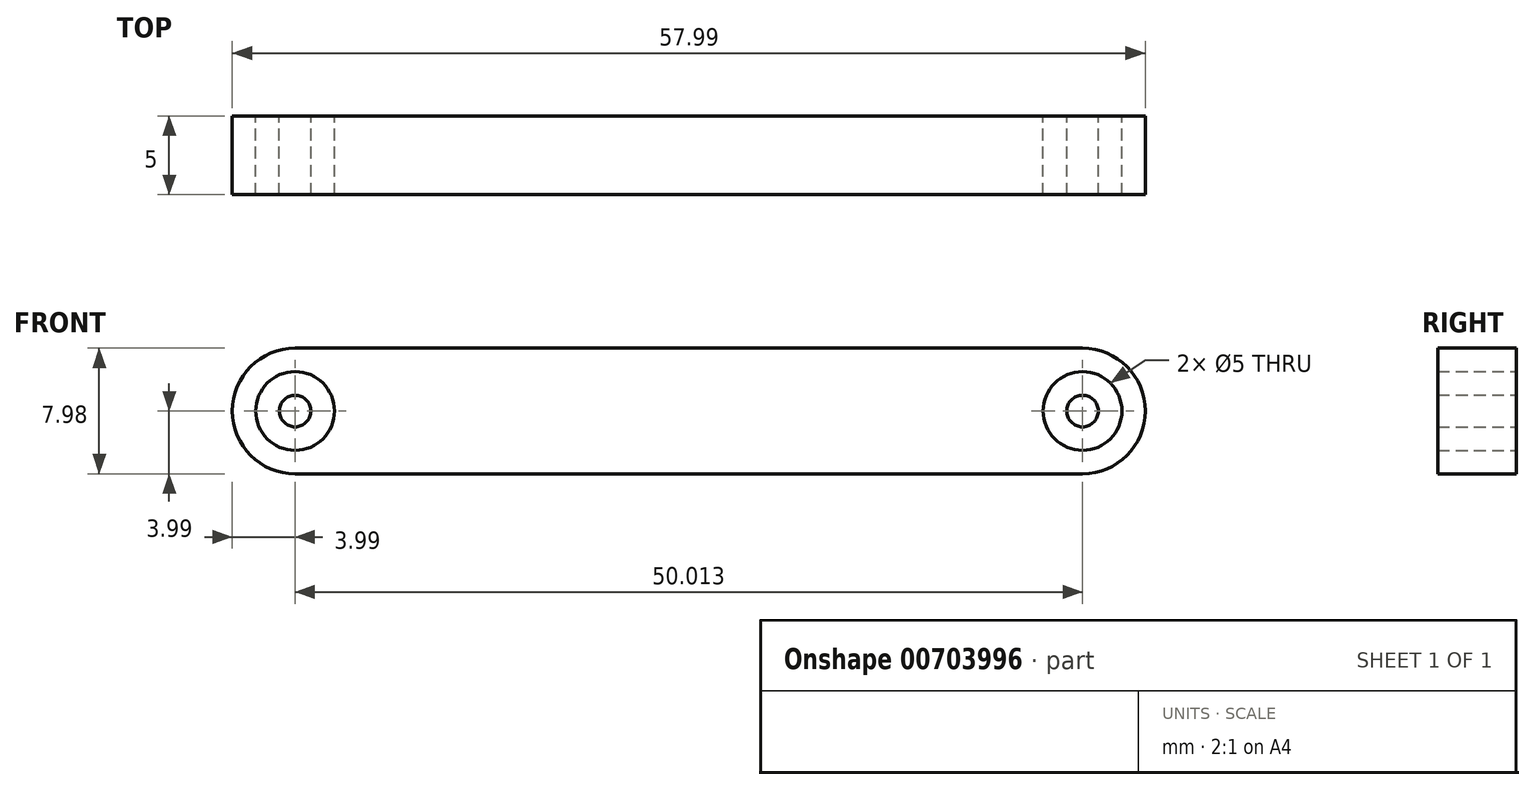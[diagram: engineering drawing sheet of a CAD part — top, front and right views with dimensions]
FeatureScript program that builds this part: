
annotation { "Feature Type Name" : "Feature", "Feature Type Description" : "" }
export const myFeature = defineFeature(function(context is Context, id is Id, definition is map)
    precondition{}
    {
        {
            var Q0;
            Q0=qCreatedBy(makeId("Front.planeOp"),FACE);
            var sketch = newSketch(context, id + "F0", { "sketchPlane" : qUnion([Q0])});
            skCircle(sketch, "E0", {"center": v(0, 0) * mm, "radius": 2.5 * mm});
            skCircle(sketch, "E1", {"center": v(0, 0) * mm, "radius": 1 * mm});
            skArc(sketch, "E2", {"start": v(0, -3.99) * mm, "mid": v(-3.99, 0) * mm, "end": v(0, 3.99) * mm});
            skCircle(sketch, "E3", {"center": v(50.01, 0) * mm, "radius": 1 * mm});
            skCircle(sketch, "E4", {"center": v(50.01, 0) * mm, "radius": 2.5 * mm});
            skArc(sketch, "E5", {"start": v(50.01, -3.99) * mm, "mid": v(54, 0) * mm, "end": v(50.01, 3.99) * mm});
            skLineSegment(sketch, "E6", {"start": v(0, 3.99) * mm, "end": v(50.01, 3.99) * mm});
            skLineSegment(sketch, "E7", {"start": v(0, -3.99) * mm, "end": v(50.01, -3.99) * mm});
            skSolve(sketch);
        }
        {
            var Q0;
            Q0=makeQuery(id+"F0.imprint","IMPRINT",FACE,{"disambiguationData":[TD([[makeQuery(id+"F0.imprint","IMPRINT",EDGE,{"derivedFrom":sQuery(id+"F0.wireOp",EDGE,"E0")}),-1.0]])]});
            var Q1;
            Q1=makeQuery(id+"F0.imprint","IMPRINT",FACE,{"disambiguationData":[TD([[makeQuery(id+"F0.imprint","IMPRINT",EDGE,{"derivedFrom":sQuery(id+"F0.wireOp",EDGE,"E1")}),1.0]])]});
            var Q2;
            Q2=makeQuery(id+"F0.imprint","IMPRINT",FACE,{"disambiguationData":[TD([[makeQuery(id+"F0.imprint","IMPRINT",EDGE,{"derivedFrom":sQuery(id+"F0.wireOp",EDGE,"E3")}),1.0]])]});
            extrude(context, id + "F1", {"entities" : qUnion([Q0, Q1, Q2]), "depth" : 5 * mm, "offsetDistance" : 25.4 * mm});
        }
    });
